# Revit family: Drain_Bathtub-DXV-D1640305_Series
name_source: partatom
category: Plumbing Fixtures
units: mm (PartAtom-declared; Revit-internal decimal feet)

## family parameters
Cut with Voids When Loaded = No
Host = Face
OmniClass Number = 23.45.55.21
OmniClass Title = Drains (Wastes)
Part Type = Normal
Room Calculation Point = No
Round Connector Dimension = Use Diameter
Shared = Yes

## types (2) — shared parameters
Assembly Code = C1030200
CW Connection = No
Default Elevation = 0"
Description = DEEP SOAK DRAIN
HW Connection = No
Installation Type = Floor Mount
Manufacturer = DXV
Price = Prices may vary. Please consult Manufacturer Representative for most up-to-date price list.
URL = https://www.dxv.com
Vent Connection = No
WFU = 4
Waste Connection = Yes
Waste Connection Diameter = 1 1/2"
Waste Connection Radius = 3/4"
Width = 2 13/16"
zero-valued in all types: CWFU, HWFU

## per-type parameters (varying)
| type | Drain Length | Drain Length Constraint | Finish | Height | Length | Material | Overflow Height | Overflow Height Constraint |
| D1640305.002 | 6 1/2" | 6 1/2" | Metal-DXV-002-Polished Chrome | 21" | 6 1/2" | Metal-DXV-002-Polished Chrome | 17" | 17" |
| D1640305.295 | 9" | 9" | Metal-DXV-295-Brushed Nickel | 23 1/2" | 9" | Metal-DXV-295-Brushed Nickel | 19 1/2" | 19 1/2" |

note: column(s) folded — value = type name in every type: Model

## geometry (parser evidence)
native form markers: Sweep x3
no freeform markers — native parametric forms only
